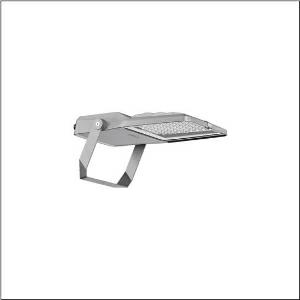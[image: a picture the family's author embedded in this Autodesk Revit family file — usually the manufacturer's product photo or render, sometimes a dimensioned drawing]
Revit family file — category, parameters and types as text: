
# Revit family: floodlight_fl_21_iq_mini___pl43_5xa7771b2a1a_26ba
name_source: partatom
category: Lighting Fixtures
units: mm (PartAtom-declared; Revit-internal decimal feet)

## family parameters
Cut with Voids When Loaded = No
Host = Face
Light Source = No
Part Type = Normal
Room Calculation Point = No
Round Connector Dimension = Use Diameter
Shared = No

## types (1)
- --- (1 x LED, 6400 lm, 45.5 W, 3000K)
    Apparent Load = 46 VA
    CIE Flux Codes = 27 78 99 100 100
    Color Rendering = 70
    Color Temperature = 3000K
    Default Elevation = 1800 mm
    Description = Floodlight FL 21 iQ mini, floodlight, primary light control with lens, of PMMA, primary optical cover: protective disc, of toughened safety glass, transparent, light distribution: PL43, light emission: direct distribution, installation type: surface-mounted, LED, High Power LED, rated luminous flux: 6.400lm, luminous efficacy: 141lm/W, light colour: 730, colour temperature: 3000K, control gear: iQ Comfort/DALI, control: Auto-Match, Temp-Guard, Lumen-Switch, Night-Set, Smart-Wire, Light-Fading, Desk-Remote (wireless, voltage-free reading and setting of iQ features in the workshop via application-optimized NFC function/RFID function), optimised constant luminous flux control (CLO 2.0), with terminal, 6-pole, mains connection: 220..240V, AC, 50/60Hz, start of lifetime: 46W, end of service life: 48W, reduction: 22W, luminaire housing, of diecast aluminium, powder-coated, Siteco® metallic grey (DB 702S), corrosivity category C5 mid according to DIN EN ISO 12944, suitable for swimming pools, chlorine-resistant, sealing non-destructively replaceable, mounting bracket, of steel, galvanised, powder-coated, Siteco® metallic grey (DB 702S), protection rating (complete): IP66, insulation class (complete): insulation class II (safety insulation), certification: CE, ENEC, VDE, protection symbol: D, impact resistance: IK08, permissible operating ambient temperature: -40..+40°C, permissible operating ambient temperature for outdoor applications: -40..+50°C, standard: DIN EN 12944, LABS conformity tested according to VDMA 24364:2018-05, packaging unit: 1 piece

Light Distribution: PL43
    Height = 70 mm
    Lamp = 1 x LED
    Lamp Light Flux = 6400 lm
    Lamp Power = 45.5 W
    Lamp count = 1
    Length = 485 mm
    Luminous efficacy = 141 lm/W
    Manufacturer = Siteco
    ModVariant = No
    Model = 5XA7771B2A1A
    Mounting Place = Wall
    Mounting Type = Surface mounted
    Number of Poles = 1
    OnlyDefault = Yes
    Power Factor = 1
    Product Name = Floodlight FL 21 iQ mini | PL43
    Product group = floodlight | wall mounted
    ProductGroupID = 2001
    Protection Class = Protection class II
    Protection Degree = IP 66
    RLX_Detail_Level = 1
    RLX_Emergency_Light_Flux = 0 lm
    RLX_Emergency_Type = 0
    RLX_Emergency_Type_DB = No
    RlxData = <blob elided: 96033 chars, md5=5999251e>
    Socket = socket
    Standby Power = 0 W
    System Light Flux = 6400 lm
    System Power = 46 W
    Type Comments = factory setting: luminous flux: 100 % | dim-lin: 254 | 463 mA
    Type Image = l_1006845.jpg
    URL = http://relux.com
    VarID = @adj_163078
    Voltage = 0 V
    Weight = 0.00 kg
    Width = 337 mm

## geometry (parser evidence)
native form markers: Blend x4, Sweep x11
no freeform markers — native parametric forms only
